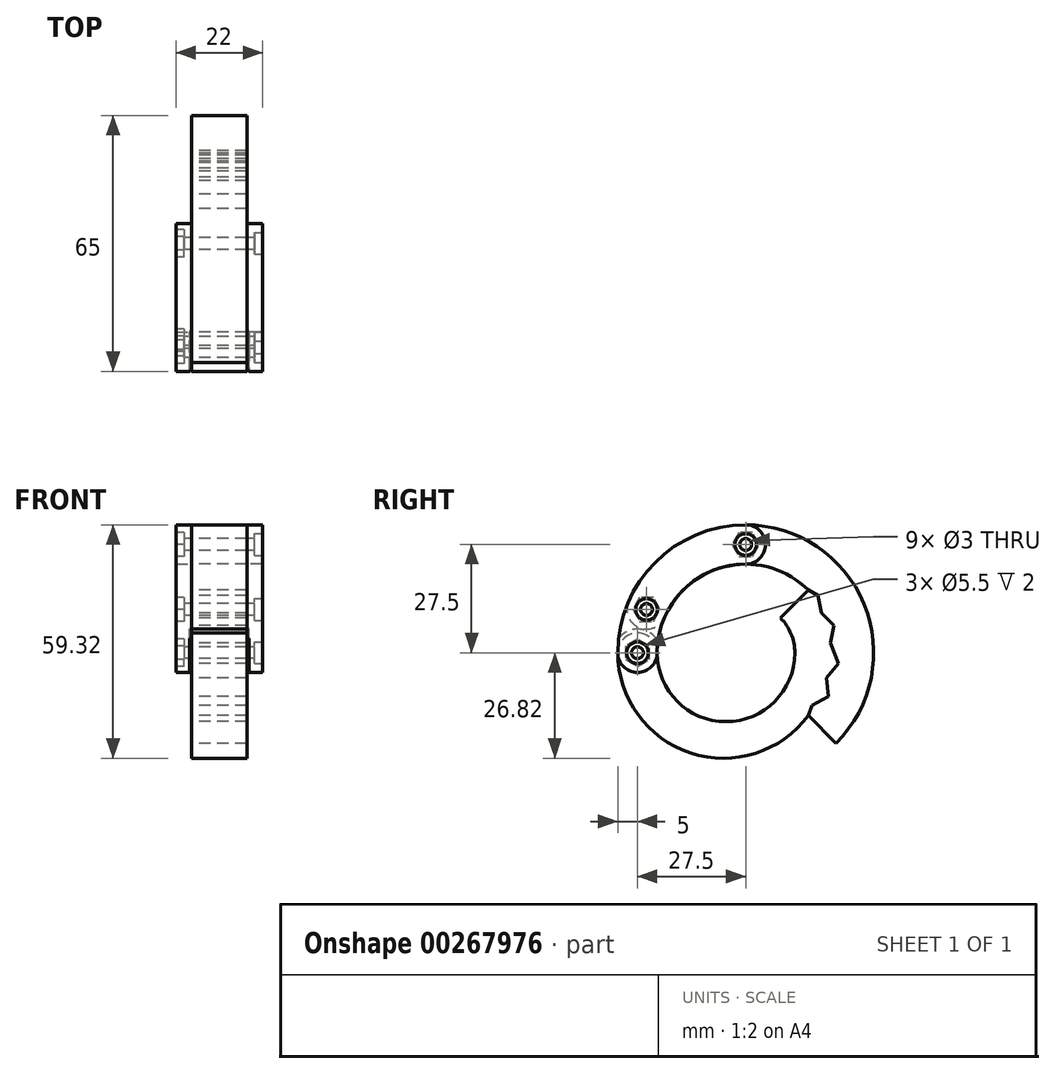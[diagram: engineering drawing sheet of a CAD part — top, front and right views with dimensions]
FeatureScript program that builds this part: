
annotation { "Feature Type Name" : "Feature", "Feature Type Description" : "" }
export const myFeature = defineFeature(function(context is Context, id is Id, definition is map)
    precondition{}
    {
        {
            var Q0;
            Q0=qCreatedBy(makeId("Right.planeOp"),FACE);
            var sketch = newSketch(context, id + "F0", { "sketchPlane" : qUnion([Q0])});
            skCircle(sketch, "E0", {"center": v(0, 0) * mm, "radius": 12.5 * mm, "construction": true});
            skCircle(sketch, "E1", {"center": v(0, 0) * mm, "radius": 22.5 * mm, "construction": true});
            skCircle(sketch, "E2", {"center": v(-27.5, 0) * mm, "radius": 5 * mm});
            skArc(sketch, "E3", {"start": v(-32.5, 0) * mm, "mid": v(-14.05, -25.48) * mm, "end": v(15.9, -15.9) * mm});
            skArc(sketch, "E4", {"start": v(-22.5, 0) * mm, "mid": v(-5, -17.5) * mm, "end": v(12.5, 0) * mm});
            skArc(sketch, "E5", {"start": v(22.98, -22.98) * mm, "mid": v(12.44, 30.03) * mm, "end": v(-32.5, 0) * mm});
            skPoint(sketch, "E6", {"position": v(0, -12.5) * mm});
            skArc(sketch, "E7", {"start": v(12.5, 0) * mm, "mid": v(11.55, 4.78) * mm, "end": v(8.84, 8.84) * mm});
            skLineSegment(sketch, "E8", {"start": v(0, 0) * mm, "end": v(8.84, 8.84) * mm, "construction": true});
            skLineSegment(sketch, "E9", {"start": v(0, 0) * mm, "end": v(12.5, 0) * mm, "construction": true});
            skLineSegment(sketch, "E10", {"start": v(8.84, 8.84) * mm, "end": v(15.9, 15.9) * mm});
            skLineSegment(sketch, "E11", {"start": v(0, 0) * mm, "end": v(22.98, -22.98) * mm, "construction": true});
            skLineSegment(sketch, "E12", {"start": v(22.98, -22.98) * mm, "end": v(15.9, -15.9) * mm});
            skLineSegment(sketch, "E13", {"start": v(15.9, -15.9) * mm, "end": v(16.84, -13.36) * mm});
            skLineSegment(sketch, "E14", {"start": v(16.84, -13.36) * mm, "end": v(20.96, -11.05) * mm});
            skLineSegment(sketch, "E15", {"start": v(20.96, -11.05) * mm, "end": v(20.54, -6.36) * mm});
            skLineSegment(sketch, "E16", {"start": v(0, 0) * mm, "end": v(17.63, -13.98) * mm, "construction": true});
            skLineSegment(sketch, "E17", {"start": v(0, 0) * mm, "end": v(28.75, -15.16) * mm, "construction": true});
            skLineSegment(sketch, "E18", {"start": v(0, 0) * mm, "end": v(21.5, -6.65) * mm, "construction": true});
            skLineSegment(sketch, "E19", {"start": v(0, 0) * mm, "end": v(32.29, -3.72) * mm, "construction": true});
            skLineSegment(sketch, "E20", {"start": v(20.54, -6.36) * mm, "end": v(23.54, -2.72) * mm});
            skLineSegment(sketch, "E21", {"start": v(8.84, -8.84) * mm, "end": v(9.8, -7.77) * mm, "construction": true});
            skLineSegment(sketch, "E22", {"start": v(11.06, -5.83) * mm, "end": v(9.8, -7.77) * mm, "construction": true});
            skLineSegment(sketch, "E23", {"start": v(11.94, -3.7) * mm, "end": v(11.06, -5.83) * mm, "construction": true});
            skLineSegment(sketch, "E24", {"start": v(12.42, -1.43) * mm, "end": v(11.94, -3.7) * mm, "construction": true});
            skLineSegment(sketch, "E25", {"start": v(12.5, 0) * mm, "end": v(12.42, -1.43) * mm, "construction": true});
            skLineSegment(sketch, "E26", {"start": v(0, 0) * mm, "end": v(22.35, 2.58) * mm, "construction": true});
            skLineSegment(sketch, "E27", {"start": v(0, 0) * mm, "end": v(31.05, 9.6) * mm, "construction": true});
            skLineSegment(sketch, "E28", {"start": v(0, 0) * mm, "end": v(19.9, 10.5) * mm, "construction": true});
            skLineSegment(sketch, "E29", {"start": v(0, 0) * mm, "end": v(25.46, 20.2) * mm, "construction": true});
            skLineSegment(sketch, "E30", {"start": v(8.84, 8.84) * mm, "end": v(9.8, 7.77) * mm, "construction": true});
            skLineSegment(sketch, "E31", {"start": v(9.8, 7.77) * mm, "end": v(11.06, 5.83) * mm, "construction": true});
            skLineSegment(sketch, "E32", {"start": v(11.06, 5.83) * mm, "end": v(11.94, 3.7) * mm, "construction": true});
            skLineSegment(sketch, "E33", {"start": v(11.94, 3.7) * mm, "end": v(12.42, 1.43) * mm, "construction": true});
            skLineSegment(sketch, "E34", {"start": v(12.42, 1.43) * mm, "end": v(12.5, 0) * mm, "construction": true});
            skLineSegment(sketch, "E35", {"start": v(21.55, 2.49) * mm, "end": v(22.45, 6.95) * mm});
            skLineSegment(sketch, "E36", {"start": v(22.45, 6.95) * mm, "end": v(19.19, 10.12) * mm});
            skLineSegment(sketch, "E37", {"start": v(19.19, 10.12) * mm, "end": v(18.41, 14.6) * mm});
            skLineSegment(sketch, "E38", {"start": v(18.41, 14.6) * mm, "end": v(15.9, 15.9) * mm});
            skLineSegment(sketch, "E39", {"start": v(23.54, -2.72) * mm, "end": v(22.5, 0) * mm});
            skLineSegment(sketch, "E40", {"start": v(22.5, 0) * mm, "end": v(21.55, 2.49) * mm});
            skPoint(sketch, "E41", {"position": v(20.82, 8.53) * mm});
            skPoint(sketch, "E42", {"position": v(18.8, 12.36) * mm});
            skPoint(sketch, "E43", {"position": v(22, 4.72) * mm});
            skPoint(sketch, "E44", {"position": v(22.04, -4.54) * mm});
            skPoint(sketch, "E45", {"position": v(20.75, -8.7) * mm});
            skPoint(sketch, "E46", {"position": v(18.9, -12.2) * mm});
            skArc(sketch, "E47", {"start": v(-22.5, 0) * mm, "mid": v(-8.61, 20.79) * mm, "end": v(15.9, 15.9) * mm});
            skLineSegment(sketch, "E48", {"start": v(0, 0) * mm, "end": v(-20.2, 25.46) * mm, "construction": true});
            skCircle(sketch, "E49", {"center": v(-25.2, 11) * mm, "radius": 5 * mm});
            skCircle(sketch, "E50", {"center": v(0, 27.5) * mm, "radius": 5 * mm});
            skCircle(sketch, "E51", {"center": v(-27.5, 0) * mm, "radius": 6 * mm});
            skSolve(sketch);
        }
        {
            var Q0;
            Q0=qCreatedBy(makeId("Right.planeOp"),FACE);
            var sketch = newSketch(context, id + "F1", { "sketchPlane" : qUnion([Q0])});
            skCircle(sketch, "E52", {"center": v(-27.5, 0) * mm, "radius": 1.5 * mm});
            skCircle(sketch, "E53", {"center": v(-25.2, 11) * mm, "radius": 1.5 * mm});
            skCircle(sketch, "E54", {"center": v(0, 27.5) * mm, "radius": 1.5 * mm});
            skSolve(sketch);
        }
        {
            var Q0;
            {var subQ0=sQuery(id+"F0.wireOp",EDGE,"E50");var subQ1=makeQuery(id+"F0.imprint","INTERSECT",VERTEX,{"derivedFrom":[sQuery(id+"F0.wireOp",EDGE,"E5"),subQ0]});Q0=makeQuery(id+"F0.imprint","IMPRINT",FACE,{"disambiguationData":[TD([[makeQuery(id+"F0.imprint","IMPRINT",EDGE,{"disambiguationData":[TD([[subQ1,-1.0]])],"derivedFrom":subQ0}),1.0]])]});}
            var Q1;
            {var subQ0=sQuery(id+"F0.wireOp",EDGE,"E50");var subQ1=sQuery(id+"F0.wireOp",EDGE,"E5");var subQ2=makeQuery(id+"F0.imprint","INTERSECT",VERTEX,{"derivedFrom":[subQ1,subQ0]});Q1=makeQuery(id+"F0.imprint","IMPRINT",FACE,{"disambiguationData":[TD([[makeQuery(id+"F0.imprint","IMPRINT",EDGE,{"disambiguationData":[TD([[subQ2,-1.0]])],"derivedFrom":subQ1}),1.0]])]});}
            var Q2;
            {var subQ0=sQuery(id+"F0.wireOp",EDGE,"E49");var subQ1=makeQuery(id+"F0.imprint","INTERSECT",VERTEX,{"derivedFrom":[sQuery(id+"F0.wireOp",EDGE,"E5"),subQ0]});Q2=makeQuery(id+"F0.imprint","IMPRINT",FACE,{"disambiguationData":[TD([[makeQuery(id+"F0.imprint","IMPRINT",EDGE,{"disambiguationData":[TD([[subQ1,-1.0]])],"derivedFrom":subQ0}),1.0]])]});}
            var Q3;
            {var subQ0=sQuery(id+"F0.wireOp",EDGE,"E5");var subQ5=sQuery(id+"F0.wireOp",EDGE,"E49");var subQ6=makeQuery(id+"F0.imprint","INTERSECT",VERTEX,{"derivedFrom":[subQ0,subQ5]});Q3=makeQuery(id+"F0.imprint","IMPRINT",FACE,{"disambiguationData":[TD([[makeQuery(id+"F0.imprint","IMPRINT",EDGE,{"disambiguationData":[TD([[subQ6,-1.0]])],"derivedFrom":subQ5}),-1.0]])]});}
            var Q4;
            {var subQ0=sQuery(id+"F0.wireOp",EDGE,"E2");var subQ1=makeQuery(id+"F0.imprint","INTERSECT",VERTEX,{"derivedFrom":[subQ0,sQuery(id+"F0.wireOp",EDGE,"E3"),sQuery(id+"F0.wireOp",EDGE,"E5")]});Q4=makeQuery(id+"F0.imprint","IMPRINT",FACE,{"disambiguationData":[TD([[makeQuery(id+"F0.imprint","IMPRINT",EDGE,{"disambiguationData":[TD([[subQ1,1.0]])],"derivedFrom":subQ0}),1.0]])]});}
            var Q5;
            {var subQ0=sQuery(id+"F0.wireOp",EDGE,"E5");var subQ5=sQuery(id+"F0.wireOp",EDGE,"E51");var subQ7=makeQuery(id+"F0.imprint","INTERSECT",VERTEX,{"derivedFrom":[subQ0,subQ5]});Q5=makeQuery(id+"F0.imprint","IMPRINT",FACE,{"disambiguationData":[TD([[makeQuery(id+"F0.imprint","IMPRINT",EDGE,{"disambiguationData":[TD([[subQ7,1.0]])],"derivedFrom":subQ5}),1.0]])]});}
            extrude(context, id + "F2", {"entities" : qUnion([Q0, Q1, Q2, Q3, Q4, Q5]), "depth" : 11 * mm});
        }
        {
            var Q0;
            {var subQ0=sQuery(id+"F0.wireOp",EDGE,"E5");var subQ5=sQuery(id+"F0.wireOp",EDGE,"E49");var subQ6=makeQuery(id+"F0.imprint","INTERSECT",VERTEX,{"derivedFrom":[subQ0,subQ5]});Q0=makeQuery(id+"F0.imprint","IMPRINT",FACE,{"disambiguationData":[TD([[makeQuery(id+"F0.imprint","IMPRINT",EDGE,{"disambiguationData":[TD([[subQ6,-1.0]])],"derivedFrom":subQ5}),-1.0]])]});}
            var Q1;
            {var subQ0=sQuery(id+"F0.wireOp",EDGE,"E49");var subQ1=makeQuery(id+"F0.imprint","INTERSECT",VERTEX,{"derivedFrom":[sQuery(id+"F0.wireOp",EDGE,"E5"),subQ0]});Q1=makeQuery(id+"F0.imprint","IMPRINT",FACE,{"disambiguationData":[TD([[makeQuery(id+"F0.imprint","IMPRINT",EDGE,{"disambiguationData":[TD([[subQ1,-1.0]])],"derivedFrom":subQ0}),1.0]])]});}
            var Q2;
            {var subQ0=sQuery(id+"F0.wireOp",EDGE,"E50");var subQ1=sQuery(id+"F0.wireOp",EDGE,"E5");var subQ2=makeQuery(id+"F0.imprint","INTERSECT",VERTEX,{"derivedFrom":[subQ1,subQ0]});Q2=makeQuery(id+"F0.imprint","IMPRINT",FACE,{"disambiguationData":[TD([[makeQuery(id+"F0.imprint","IMPRINT",EDGE,{"disambiguationData":[TD([[subQ2,-1.0]])],"derivedFrom":subQ1}),1.0]])]});}
            var Q3;
            {var subQ0=sQuery(id+"F0.wireOp",EDGE,"E50");var subQ1=makeQuery(id+"F0.imprint","INTERSECT",VERTEX,{"derivedFrom":[sQuery(id+"F0.wireOp",EDGE,"E5"),subQ0]});Q3=makeQuery(id+"F0.imprint","IMPRINT",FACE,{"disambiguationData":[TD([[makeQuery(id+"F0.imprint","IMPRINT",EDGE,{"disambiguationData":[TD([[subQ1,-1.0]])],"derivedFrom":subQ0}),1.0]])]});}
            var Q4;
            {var subQ0=sQuery(id+"F0.wireOp",EDGE,"E2");var subQ1=makeQuery(id+"F0.imprint","INTERSECT",VERTEX,{"derivedFrom":[subQ0,sQuery(id+"F0.wireOp",EDGE,"E3"),sQuery(id+"F0.wireOp",EDGE,"E5")]});Q4=makeQuery(id+"F0.imprint","IMPRINT",FACE,{"disambiguationData":[TD([[makeQuery(id+"F0.imprint","IMPRINT",EDGE,{"disambiguationData":[TD([[subQ1,1.0]])],"derivedFrom":subQ0}),1.0]])]});}
            var Q5;
            {var subQ0=sQuery(id+"F0.wireOp",EDGE,"E5");var subQ5=sQuery(id+"F0.wireOp",EDGE,"E51");var subQ7=makeQuery(id+"F0.imprint","INTERSECT",VERTEX,{"derivedFrom":[subQ0,subQ5]});Q5=makeQuery(id+"F0.imprint","IMPRINT",FACE,{"disambiguationData":[TD([[makeQuery(id+"F0.imprint","IMPRINT",EDGE,{"disambiguationData":[TD([[subQ7,1.0]])],"derivedFrom":subQ5}),1.0]])]});}
            extrude(context, id + "F3", {"entities" : qUnion([Q0, Q1, Q2, Q3, Q4, Q5]), "oppositeDirection" : true, "depth" : 11 * mm});
        }
        {
            var Q0;
            {var subQ0=sQuery(id+"F0.wireOp",EDGE,"E50");var subQ1=makeQuery(id+"F0.imprint","INTERSECT",VERTEX,{"derivedFrom":[sQuery(id+"F0.wireOp",EDGE,"E5"),subQ0]});Q0=makeQuery(id+"F0.imprint","IMPRINT",FACE,{"disambiguationData":[TD([[makeQuery(id+"F0.imprint","IMPRINT",EDGE,{"disambiguationData":[TD([[subQ1,-1.0]])],"derivedFrom":subQ0}),1.0]])]});}
            var Q1;
            {var subQ0=sQuery(id+"F0.wireOp",EDGE,"E50");var subQ1=sQuery(id+"F0.wireOp",EDGE,"E5");var subQ2=makeQuery(id+"F0.imprint","INTERSECT",VERTEX,{"derivedFrom":[subQ1,subQ0]});Q1=makeQuery(id+"F0.imprint","IMPRINT",FACE,{"disambiguationData":[TD([[makeQuery(id+"F0.imprint","IMPRINT",EDGE,{"disambiguationData":[TD([[subQ2,-1.0]])],"derivedFrom":subQ1}),1.0]])]});}
            var Q2;
            {var subQ0=sQuery(id+"F0.wireOp",EDGE,"E49");var subQ1=makeQuery(id+"F0.imprint","INTERSECT",VERTEX,{"derivedFrom":[sQuery(id+"F0.wireOp",EDGE,"E5"),subQ0]});Q2=makeQuery(id+"F0.imprint","IMPRINT",FACE,{"disambiguationData":[TD([[makeQuery(id+"F0.imprint","IMPRINT",EDGE,{"disambiguationData":[TD([[subQ1,-1.0]])],"derivedFrom":subQ0}),1.0]])]});}
            var Q3;
            {var subQ0=sQuery(id+"F0.wireOp",EDGE,"E5");var subQ5=sQuery(id+"F0.wireOp",EDGE,"E49");var subQ6=makeQuery(id+"F0.imprint","INTERSECT",VERTEX,{"derivedFrom":[subQ0,subQ5]});Q3=makeQuery(id+"F0.imprint","IMPRINT",FACE,{"disambiguationData":[TD([[makeQuery(id+"F0.imprint","IMPRINT",EDGE,{"disambiguationData":[TD([[subQ6,-1.0]])],"derivedFrom":subQ5}),-1.0]])]});}
            var Q4;
            {var subQ0=sQuery(id+"F0.wireOp",EDGE,"E2");var subQ1=makeQuery(id+"F0.imprint","INTERSECT",VERTEX,{"derivedFrom":[subQ0,sQuery(id+"F0.wireOp",EDGE,"E3"),sQuery(id+"F0.wireOp",EDGE,"E5")]});Q4=makeQuery(id+"F0.imprint","IMPRINT",FACE,{"disambiguationData":[TD([[makeQuery(id+"F0.imprint","IMPRINT",EDGE,{"disambiguationData":[TD([[subQ1,1.0]])],"derivedFrom":subQ0}),1.0]])]});}
            var Q5;
            {var subQ0=sQuery(id+"F0.wireOp",EDGE,"E5");var subQ5=sQuery(id+"F0.wireOp",EDGE,"E51");var subQ7=makeQuery(id+"F0.imprint","INTERSECT",VERTEX,{"derivedFrom":[subQ0,subQ5]});Q5=makeQuery(id+"F0.imprint","IMPRINT",FACE,{"disambiguationData":[TD([[makeQuery(id+"F0.imprint","IMPRINT",EDGE,{"disambiguationData":[TD([[subQ7,1.0]])],"derivedFrom":subQ5}),1.0]])]});}
            extrude(context, id + "F4", {"entities" : qUnion([Q0, Q1, Q2, Q3, Q4, Q5]), "operationType" : NewBodyOperationType.REMOVE, "endBound" : BoundingType.SYMMETRIC, "oppositeDirection" : true, "depth" : 14 * mm});
        }
        {
            var Q0;
            {var subQ0=sQuery(id+"F0.wireOp",EDGE,"E3");var subQ5=sQuery(id+"F0.wireOp",EDGE,"E51");var subQ6=makeQuery(id+"F0.imprint","INTERSECT",VERTEX,{"derivedFrom":[subQ0,subQ5]});Q0=makeQuery(id+"F0.imprint","IMPRINT",FACE,{"disambiguationData":[TD([[makeQuery(id+"F0.imprint","IMPRINT",EDGE,{"disambiguationData":[TD([[subQ6,-1.0]])],"derivedFrom":subQ5}),1.0]])]});}
            var Q1;
            {var subQ0=sQuery(id+"F0.wireOp",EDGE,"E2");var subQ1=makeQuery(id+"F0.imprint","INTERSECT",VERTEX,{"derivedFrom":[subQ0,sQuery(id+"F0.wireOp",EDGE,"E3"),sQuery(id+"F0.wireOp",EDGE,"E5")]});Q1=makeQuery(id+"F0.imprint","IMPRINT",FACE,{"disambiguationData":[TD([[makeQuery(id+"F0.imprint","IMPRINT",EDGE,{"disambiguationData":[TD([[subQ1,1.0]])],"derivedFrom":subQ0}),1.0]])]});}
            var Q2;
            {var subQ0=sQuery(id+"F0.wireOp",EDGE,"E5");var subQ5=sQuery(id+"F0.wireOp",EDGE,"E51");var subQ7=makeQuery(id+"F0.imprint","INTERSECT",VERTEX,{"derivedFrom":[subQ0,subQ5]});Q2=makeQuery(id+"F0.imprint","IMPRINT",FACE,{"disambiguationData":[TD([[makeQuery(id+"F0.imprint","IMPRINT",EDGE,{"disambiguationData":[TD([[subQ7,1.0]])],"derivedFrom":subQ5}),1.0]])]});}
            var Q3;
            {var subQ1=sQuery(id+"F0.wireOp",EDGE,"E4");var subQ3=sQuery(id+"F0.wireOp",EDGE,"E51");var subQ4=makeQuery(id+"F0.imprint","INTERSECT",VERTEX,{"derivedFrom":[subQ1,subQ3]});Q3=makeQuery(id+"F0.imprint","IMPRINT",FACE,{"disambiguationData":[TD([[makeQuery(id+"F0.imprint","IMPRINT",EDGE,{"disambiguationData":[TD([[subQ4,-1.0]])],"derivedFrom":subQ3}),1.0]])]});}
            var Q4;
            {var subQ1=sQuery(id+"F0.wireOp",EDGE,"E3");var subQ3=sQuery(id+"F0.wireOp",EDGE,"E51");var subQ4=makeQuery(id+"F0.imprint","INTERSECT",VERTEX,{"derivedFrom":[subQ1,subQ3]});Q4=makeQuery(id+"F0.imprint","IMPRINT",FACE,{"disambiguationData":[TD([[makeQuery(id+"F0.imprint","IMPRINT",EDGE,{"disambiguationData":[TD([[subQ4,1.0]])],"derivedFrom":subQ3}),1.0]])]});}
            extrude(context, id + "F5", {"entities" : qUnion([Q0, Q1, Q2, Q3, Q4]), "operationType" : NewBodyOperationType.REMOVE, "endBound" : BoundingType.SYMMETRIC, "depth" : 15 * mm});
        }
        {
            var Q0;
            {var subQ0=sQuery(id+"F0.wireOp",EDGE,"E2");var subQ1=makeQuery(id+"F0.imprint","INTERSECT",VERTEX,{"derivedFrom":[subQ0,sQuery(id+"F0.wireOp",EDGE,"E3"),sQuery(id+"F0.wireOp",EDGE,"E5")]});Q0=makeQuery(id+"F0.imprint","IMPRINT",FACE,{"disambiguationData":[TD([[makeQuery(id+"F0.imprint","IMPRINT",EDGE,{"disambiguationData":[TD([[subQ1,1.0]])],"derivedFrom":subQ0}),1.0]])]});}
            var Q1;
            {var subQ1=sQuery(id+"F0.wireOp",EDGE,"E3");Q1=makeQuery(id+"F0.imprint","IMPRINT",FACE,{"disambiguationData":[TD([[makeQuery(id+"F0.imprint","IMPRINT",EDGE,{"derivedFrom":subQ1}),1.0]])]});}
            var Q2;
            {var subQ0=sQuery(id+"F0.wireOp",EDGE,"E7");Q2=makeQuery(id+"F0.imprint","IMPRINT",FACE,{"disambiguationData":[TD([[makeQuery(id+"F0.imprint","IMPRINT",EDGE,{"derivedFrom":subQ0}),-1.0]])]});}
            extrude(context, id + "F6", {"entities" : qUnion([Q0, Q1, Q2]), "endBound" : BoundingType.SYMMETRIC, "depth" : 14 * mm});
        }
        {
            var Q0;
            {var subQ4=sQuery(id+"F0.wireOp",EDGE,"E12");Q0=makeQuery(id+"F0.imprint","IMPRINT",FACE,{"disambiguationData":[TD([[makeQuery(id+"F0.imprint","IMPRINT",EDGE,{"derivedFrom":subQ4}),-1.0]])]});}
            var Q1;
            {var subQ0=sQuery(id+"F0.wireOp",EDGE,"E50");var subQ1=makeQuery(id+"F0.imprint","INTERSECT",VERTEX,{"derivedFrom":[sQuery(id+"F0.wireOp",EDGE,"E5"),subQ0]});Q1=makeQuery(id+"F0.imprint","IMPRINT",FACE,{"disambiguationData":[TD([[makeQuery(id+"F0.imprint","IMPRINT",EDGE,{"disambiguationData":[TD([[subQ1,-1.0]])],"derivedFrom":subQ0}),1.0]])]});}
            var Q2;
            {var subQ0=sQuery(id+"F0.wireOp",EDGE,"E50");var subQ1=sQuery(id+"F0.wireOp",EDGE,"E5");var subQ2=makeQuery(id+"F0.imprint","INTERSECT",VERTEX,{"derivedFrom":[subQ1,subQ0]});Q2=makeQuery(id+"F0.imprint","IMPRINT",FACE,{"disambiguationData":[TD([[makeQuery(id+"F0.imprint","IMPRINT",EDGE,{"disambiguationData":[TD([[subQ2,-1.0]])],"derivedFrom":subQ1}),1.0]])]});}
            var Q3;
            {var subQ0=sQuery(id+"F0.wireOp",EDGE,"E49");var subQ1=makeQuery(id+"F0.imprint","INTERSECT",VERTEX,{"derivedFrom":[sQuery(id+"F0.wireOp",EDGE,"E5"),subQ0]});Q3=makeQuery(id+"F0.imprint","IMPRINT",FACE,{"disambiguationData":[TD([[makeQuery(id+"F0.imprint","IMPRINT",EDGE,{"disambiguationData":[TD([[subQ1,-1.0]])],"derivedFrom":subQ0}),1.0]])]});}
            extrude(context, id + "F7", {"entities" : qUnion([Q0, Q1, Q2, Q3]), "endBound" : BoundingType.SYMMETRIC, "depth" : 14 * mm});
        }
        {
            var Q0;
            Q0 = qSketchRegion(id + "F1", true);
            extrude(context, id + "F8", {"entities" : qUnion([Q0]), "operationType" : NewBodyOperationType.REMOVE, "endBound" : BoundingType.SYMMETRIC, "depth" : 25 * mm});
        }
        {
            var Q0;
            Q0=makeQuery(id+"F2.opExtrude","CAP_FACE",FACE,{"disambiguationData":[OSD([sQuery(id+"F0.wireOp",EDGE,"E2"),sQuery(id+"F0.wireOp",EDGE,"E5"),sQuery(id+"F0.wireOp",EDGE,"E47"),sQuery(id+"F0.wireOp",EDGE,"E50")])],"isStart":false});
            var sketch = newSketch(context, id + "F9", { "sketchPlane" : qUnion([Q0])});
            skCircle(sketch, "E55", {"center": v(-27.5, 0) * mm, "radius": 2.75 * mm});
            skCircle(sketch, "E56", {"center": v(-25.2, 11) * mm, "radius": 2.75 * mm});
            skCircle(sketch, "E57", {"center": v(0, 27.5) * mm, "radius": 2.75 * mm});
            skSolve(sketch);
        }
        {
            var Q0;
            Q0 = qSketchRegion(id + "F9", true);
            extrude(context, id + "F10", {"entities" : qUnion([Q0]), "operationType" : NewBodyOperationType.REMOVE, "oppositeDirection" : true, "depth" : 2 * mm});
        }
        {
            var Q0;
            Q0=makeQuery(id+"F3.opExtrude","CAP_FACE",FACE,{"disambiguationData":[OSD([sQuery(id+"F0.wireOp",EDGE,"E2"),sQuery(id+"F0.wireOp",EDGE,"E5"),sQuery(id+"F0.wireOp",EDGE,"E47"),sQuery(id+"F0.wireOp",EDGE,"E50")])],"isStart":false});
            var sketch = newSketch(context, id + "F11", { "sketchPlane" : qUnion([Q0])});
            skCircle(sketch, "E58.cCircle", {"center": v(27.5, 0) * mm, "radius": 3 * mm, "construction": true});
            skLineSegment(sketch, "E58.0", {"start": v(30.5, 1.73) * mm, "end": v(30.5, -1.73) * mm});
            skLineSegment(sketch, "E58.1", {"start": v(30.5, -1.73) * mm, "end": v(27.5, -3.46) * mm});
            skLineSegment(sketch, "E58.2", {"start": v(27.5, -3.46) * mm, "end": v(24.5, -1.73) * mm});
            skLineSegment(sketch, "E58.3", {"start": v(24.5, -1.73) * mm, "end": v(24.5, 1.73) * mm});
            skLineSegment(sketch, "E58.4", {"start": v(24.5, 1.73) * mm, "end": v(27.5, 3.46) * mm});
            skLineSegment(sketch, "E58.5", {"start": v(27.5, 3.46) * mm, "end": v(30.5, 1.73) * mm});
            skPoint(sketch, "E58.0.midPoint", {"position": v(30.5, 0) * mm});
            skCircle(sketch, "E59.cCircle", {"center": v(25.2, 11) * mm, "radius": 3 * mm, "construction": true});
            skLineSegment(sketch, "E59.0", {"start": v(26.94, 8) * mm, "end": v(23.47, 8) * mm});
            skLineSegment(sketch, "E59.1", {"start": v(23.47, 8) * mm, "end": v(21.74, 11) * mm});
            skLineSegment(sketch, "E59.2", {"start": v(21.74, 11) * mm, "end": v(23.47, 14) * mm});
            skLineSegment(sketch, "E59.3", {"start": v(23.47, 14) * mm, "end": v(26.94, 14) * mm});
            skLineSegment(sketch, "E59.4", {"start": v(26.94, 14) * mm, "end": v(28.67, 11) * mm});
            skLineSegment(sketch, "E59.5", {"start": v(28.67, 11) * mm, "end": v(26.94, 8) * mm});
            skPoint(sketch, "E59.0.midPoint", {"position": v(25.2, 8) * mm});
            skCircle(sketch, "E60.cCircle", {"center": v(0, 27.5) * mm, "radius": 3 * mm, "construction": true});
            skLineSegment(sketch, "E60.0", {"start": v(1.73, 24.5) * mm, "end": v(-1.73, 24.5) * mm});
            skLineSegment(sketch, "E60.1", {"start": v(-1.73, 24.5) * mm, "end": v(-3.46, 27.5) * mm});
            skLineSegment(sketch, "E60.2", {"start": v(-3.46, 27.5) * mm, "end": v(-1.73, 30.5) * mm});
            skLineSegment(sketch, "E60.3", {"start": v(-1.73, 30.5) * mm, "end": v(1.73, 30.5) * mm});
            skLineSegment(sketch, "E60.4", {"start": v(1.73, 30.5) * mm, "end": v(3.46, 27.5) * mm});
            skLineSegment(sketch, "E60.5", {"start": v(3.46, 27.5) * mm, "end": v(1.73, 24.5) * mm});
            skPoint(sketch, "E60.0.midPoint", {"position": v(0, 24.5) * mm});
            skSolve(sketch);
        }
        {
            var Q0;
            Q0 = qSketchRegion(id + "F11", true);
            extrude(context, id + "F12", {"entities" : qUnion([Q0]), "operationType" : NewBodyOperationType.REMOVE, "oppositeDirection" : true, "depth" : 2 * mm});
        }
    });
